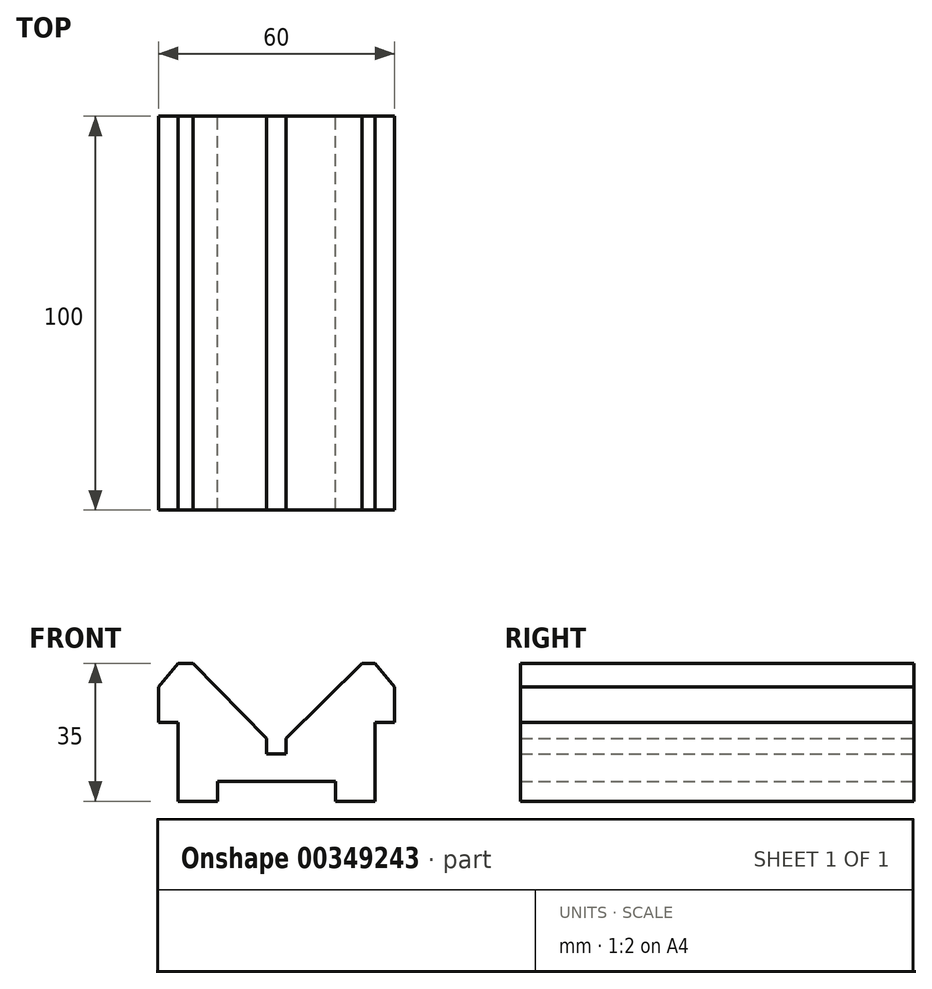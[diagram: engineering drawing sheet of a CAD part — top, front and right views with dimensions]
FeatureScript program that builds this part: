
annotation { "Feature Type Name" : "Feature", "Feature Type Description" : "" }
export const myFeature = defineFeature(function(context is Context, id is Id, definition is map)
    precondition{}
    {
        {
            var Q0;
            Q0=qCreatedBy(makeId("Front.planeOp"),FACE);
            var sketch = newSketch(context, id + "F0", { "sketchPlane" : qUnion([Q0])});
            skLineSegment(sketch, "E0", {"start": v(-25, 0) * mm, "end": v(-25, 20) * mm});
            skLineSegment(sketch, "E1.MirrorCS", {"start": v(25, 0) * mm, "end": v(25, 20) * mm});
            skLineSegment(sketch, "E2", {"start": v(-25, 20) * mm, "end": v(-30, 20) * mm});
            skLineSegment(sketch, "E3", {"start": v(-25, 35) * mm, "end": v(-21.23, 35) * mm});
            skLineSegment(sketch, "E4", {"start": v(-25, 0) * mm, "end": v(-15, 0) * mm});
            skLineSegment(sketch, "E5", {"start": v(-15, 0) * mm, "end": v(-15, 5) * mm});
            skLineSegment(sketch, "E6", {"start": v(-15, 5) * mm, "end": v(15, 5) * mm});
            skLineSegment(sketch, "E7", {"start": v(15, 5) * mm, "end": v(15, 0) * mm});
            skLineSegment(sketch, "E8", {"start": v(15, 0) * mm, "end": v(25, 0) * mm});
            skLineSegment(sketch, "E9.MirrorCS", {"start": v(25, 20) * mm, "end": v(30, 20) * mm});
            skLineSegment(sketch, "E10", {"start": v(-21.23, 35) * mm, "end": v(-2.5, 16) * mm});
            skLineSegment(sketch, "E11", {"start": v(-2.5, 16) * mm, "end": v(-2.5, 12) * mm});
            skLineSegment(sketch, "E12", {"start": v(2.5, 12) * mm, "end": v(2.5, 16) * mm});
            skLineSegment(sketch, "E13", {"start": v(2.5, 16) * mm, "end": v(21.77, 35) * mm});
            skLineSegment(sketch, "E14", {"start": v(21.77, 35) * mm, "end": v(25, 35) * mm});
            skLineSegment(sketch, "E15", {"start": v(-2.5, 12) * mm, "end": v(2.5, 12) * mm});
            skPoint(sketch, "E16.end.orphan", {"position": v(-30, 40.71) * mm});
            skPoint(sketch, "E17.MirrorCS.start.orphan", {"position": v(30, 40.71) * mm});
            skPoint(sketch, "E18.MirrorCS.start.orphan", {"position": v(30, 20) * mm});
            skLineSegment(sketch, "E19", {"start": v(-30, 20) * mm, "end": v(-30, 29) * mm});
            skLineSegment(sketch, "E20", {"start": v(-30, 29) * mm, "end": v(-25, 35) * mm});
            skLineSegment(sketch, "E21", {"start": v(30, 20) * mm, "end": v(30, 29) * mm});
            skLineSegment(sketch, "E22", {"start": v(30, 29) * mm, "end": v(25, 35) * mm});
            skSolve(sketch);
        }
        {
            var Q0;
            Q0 = qSketchRegion(id + "F0", true);
            extrude(context, id + "F1", {"entities" : qUnion([Q0]), "depth" : 100 * mm});
        }
    });
